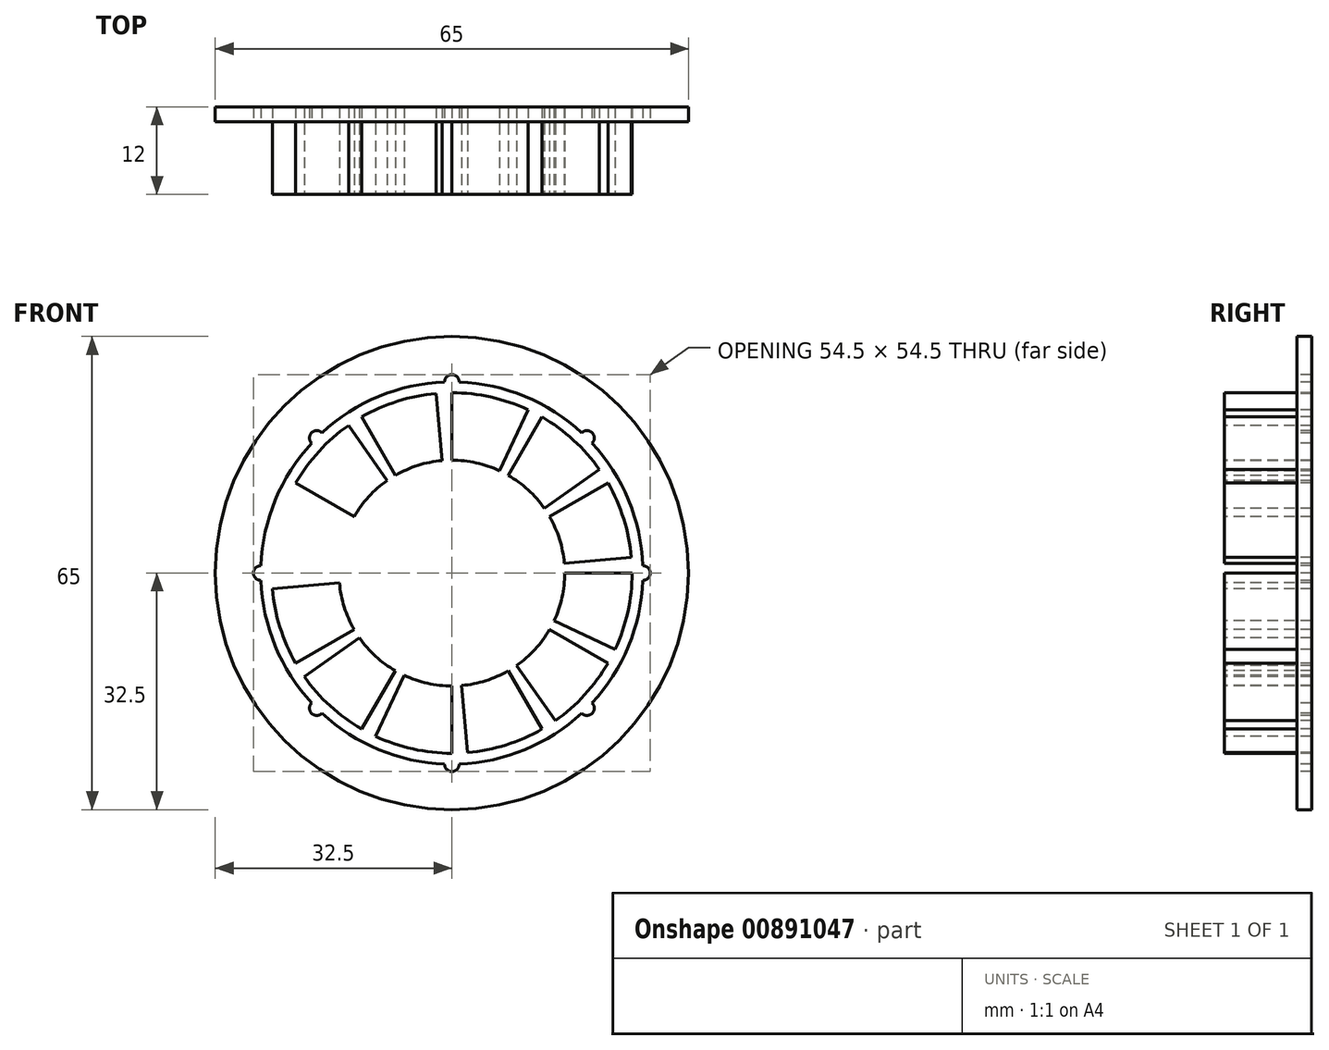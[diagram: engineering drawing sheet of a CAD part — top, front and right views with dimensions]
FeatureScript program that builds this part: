
annotation { "Feature Type Name" : "Feature", "Feature Type Description" : "" }
export const myFeature = defineFeature(function(context is Context, id is Id, definition is map)
    precondition{}
    {
        {
            var Q0;
            Q0=qCreatedBy(makeId("Front.planeOp"),FACE);
            var sketch = newSketch(context, id + "F0", { "sketchPlane" : qUnion([Q0])});
            skCircle(sketch, "E0", {"center": v(0, 0) * mm, "radius": 26.25 * mm});
            skCircle(sketch, "E1", {"center": v(0, 0) * mm, "radius": 14 * mm});
            skSolve(sketch);
        }
        {
            var Q0;
            Q0=makeQuery(id+"F0.imprint","IMPRINT",FACE,{"disambiguationData":[TD([[makeQuery(id+"F0.imprint","IMPRINT",EDGE,{"derivedFrom":sQuery(id+"F0.wireOp",EDGE,"E0")}),1.0]])]});
            extrude(context, id + "F1", {"entities" : qUnion([Q0]), "depth" : 10 * mm, "offsetDistance" : 25 * mm});
        }
        {
            var Q0;
            Q0=qCreatedBy(makeId("Front.planeOp"),FACE);
            var sketch = newSketch(context, id + "F2", { "sketchPlane" : qUnion([Q0])});
            skCircle(sketch, "E2", {"center": v(0, 0) * mm, "radius": 32.5 * mm});
            skCircle(sketch, "E3", {"center": v(0, 0) * mm, "radius": 14 * mm});
            skSolve(sketch);
        }
        {
            var Q0;
            Q0=makeQuery(id+"F2.imprint","IMPRINT",FACE,{"disambiguationData":[TD([[makeQuery(id+"F2.imprint","IMPRINT",EDGE,{"derivedFrom":sQuery(id+"F2.wireOp",EDGE,"E2")}),1.0]])]});
            extrude(context, id + "F3", {"entities" : qUnion([Q0]), "operationType" : NewBodyOperationType.ADD, "oppositeDirection" : true, "depth" : 2 * mm, "offsetDistance" : 25 * mm});
        }
        {
            var Q0;
            Q0=makeQuery(id+"F3.opExtrude","CAP_FACE",FACE,{"disambiguationData":[OSD([sQuery(id+"F2.wireOp",EDGE,"E2"),sQuery(id+"F2.wireOp",EDGE,"E3")])],"isStart":true});
            var sketch = newSketch(context, id + "F4", { "sketchPlane" : qUnion([Q0])});
            skCircle(sketch, "E4", {"center": v(0, 26.25) * mm, "radius": 1 * mm});
            skCircle(sketch, "E5", {"center": v(26.25, 0) * mm, "radius": 1 * mm});
            skCircle(sketch, "E6", {"center": v(0, -26.25) * mm, "radius": 1 * mm});
            skCircle(sketch, "E7", {"center": v(-26.25, 0) * mm, "radius": 1 * mm});
            skCircle(sketch, "E8.1.0", {"center": v(-18.56, 18.56) * mm, "radius": 1 * mm});
            skCircle(sketch, "E8.3.0", {"center": v(-18.56, -18.56) * mm, "radius": 1 * mm});
            skCircle(sketch, "E8.5.0", {"center": v(18.56, -18.56) * mm, "radius": 1 * mm});
            skCircle(sketch, "E8.7.0", {"center": v(18.56, 18.56) * mm, "radius": 1 * mm});
            skPoint(sketch, "E8.center", {"position": v(0, 0) * mm});
            skSolve(sketch);
        }
        {
            var Q0;
            Q0 = qSketchRegion(id + "F4", true);
            var Q1;
            Q1=makeQuery(id+"F1.opExtrude","CAP_FACE",FACE,{"disambiguationData":[OSD([sQuery(id+"F0.wireOp",EDGE,"E0"),sQuery(id+"F0.wireOp",EDGE,"E1")])],"isStart":false});
            extrude(context, id + "F5", {"entities" : qUnion([Q0]), "operationType" : NewBodyOperationType.ADD, "endBound" : BoundingType.UP_TO_SURFACE, "depth" : 25 * mm, "endBoundEntityFace" : qUnion([Q1]), "offsetDistance" : 25 * mm});
        }
        {
            var Q0;
            Q0=makeQuery(id+"F5.boolean.opBoolean","MERGE",FACE,{"derivedFrom":[makeQuery(id+"F1.opExtrude","CAP_FACE",FACE,{"disambiguationData":[OSD([sQuery(id+"F0.wireOp",EDGE,"E0"),sQuery(id+"F0.wireOp",EDGE,"E1")])],"isStart":false}),makeQuery(id+"F5.opExtrude","CAP_FACE",FACE,{"disambiguationData":[OSD([sQuery(id+"F4.wireOp",EDGE,"E4")])],"isStart":false}),makeQuery(id+"F5.opExtrude","CAP_FACE",FACE,{"disambiguationData":[OSD([sQuery(id+"F4.wireOp",EDGE,"E8.1.0")])],"isStart":false}),makeQuery(id+"F5.opExtrude","CAP_FACE",FACE,{"disambiguationData":[OSD([sQuery(id+"F4.wireOp",EDGE,"E7")])],"isStart":false}),makeQuery(id+"F5.opExtrude","CAP_FACE",FACE,{"disambiguationData":[OSD([sQuery(id+"F4.wireOp",EDGE,"E8.3.0")])],"isStart":false}),makeQuery(id+"F5.opExtrude","CAP_FACE",FACE,{"disambiguationData":[OSD([sQuery(id+"F4.wireOp",EDGE,"E6")])],"isStart":false}),makeQuery(id+"F5.opExtrude","CAP_FACE",FACE,{"disambiguationData":[OSD([sQuery(id+"F4.wireOp",EDGE,"E8.5.0")])],"isStart":false}),makeQuery(id+"F5.opExtrude","CAP_FACE",FACE,{"disambiguationData":[OSD([sQuery(id+"F4.wireOp",EDGE,"E5")])],"isStart":false}),makeQuery(id+"F5.opExtrude","CAP_FACE",FACE,{"disambiguationData":[OSD([sQuery(id+"F4.wireOp",EDGE,"E8.7.0")])],"isStart":false})]});
            var sketch = newSketch(context, id + "F6", { "sketchPlane" : qUnion([Q0])});
            skLineSegment(sketch, "E9", {"start": v(-24.75, 0) * mm, "end": v(-15.5, 0) * mm});
            skArc(sketch, "E10", {"start": v(-15.5, 0) * mm, "mid": v(-15.13, 3.35) * mm, "end": v(-14.05, 6.55) * mm});
            skArc(sketch, "E11", {"start": v(-24.75, 0) * mm, "mid": v(-24.16, 5.36) * mm, "end": v(-22.43, 10.46) * mm});
            skLineSegment(sketch, "E12.1.11.0", {"start": v(-22.43, 10.46) * mm, "end": v(-14.05, 6.55) * mm});
            skArc(sketch, "E13.1.0", {"start": v(-21.43, -12.37) * mm, "mid": v(-23.6, -7.44) * mm, "end": v(-24.66, -2.16) * mm});
            skLineSegment(sketch, "E13.1.1", {"start": v(-21.43, -12.37) * mm, "end": v(-13.42, -7.75) * mm});
            skLineSegment(sketch, "E13.1.2", {"start": v(-24.66, -2.16) * mm, "end": v(-15.44, -1.35) * mm});
            skArc(sketch, "E13.1.3", {"start": v(-13.42, -7.75) * mm, "mid": v(-14.78, -4.66) * mm, "end": v(-15.44, -1.35) * mm});
            skArc(sketch, "E13.2.0", {"start": v(-12.38, -21.43) * mm, "mid": v(-16.72, -18.25) * mm, "end": v(-20.27, -14.2) * mm});
            skLineSegment(sketch, "E13.2.1", {"start": v(-12.38, -21.43) * mm, "end": v(-7.75, -13.42) * mm});
            skLineSegment(sketch, "E13.2.2", {"start": v(-20.27, -14.2) * mm, "end": v(-12.7, -8.9) * mm});
            skArc(sketch, "E13.2.3", {"start": v(-7.75, -13.42) * mm, "mid": v(-10.47, -11.43) * mm, "end": v(-12.7, -8.9) * mm});
            skArc(sketch, "E13.3.0", {"start": v(0, -24.75) * mm, "mid": v(-5.36, -24.16) * mm, "end": v(-10.46, -22.43) * mm});
            skLineSegment(sketch, "E13.3.1", {"start": v(0, -24.75) * mm, "end": v(0, -15.5) * mm});
            skLineSegment(sketch, "E13.3.2", {"start": v(-10.46, -22.43) * mm, "end": v(-6.55, -14.05) * mm});
            skArc(sketch, "E13.3.3", {"start": v(0, -15.5) * mm, "mid": v(-3.35, -15.13) * mm, "end": v(-6.55, -14.05) * mm});
            skArc(sketch, "E13.4.0", {"start": v(12.37, -21.43) * mm, "mid": v(7.44, -23.6) * mm, "end": v(2.16, -24.66) * mm});
            skLineSegment(sketch, "E13.4.1", {"start": v(12.37, -21.43) * mm, "end": v(7.75, -13.42) * mm});
            skLineSegment(sketch, "E13.4.2", {"start": v(2.16, -24.66) * mm, "end": v(1.35, -15.44) * mm});
            skArc(sketch, "E13.4.3", {"start": v(7.75, -13.42) * mm, "mid": v(4.66, -14.78) * mm, "end": v(1.35, -15.44) * mm});
            skArc(sketch, "E13.5.0", {"start": v(21.43, -12.37) * mm, "mid": v(18.25, -16.72) * mm, "end": v(14.2, -20.27) * mm});
            skLineSegment(sketch, "E13.5.1", {"start": v(21.43, -12.37) * mm, "end": v(13.42, -7.75) * mm});
            skLineSegment(sketch, "E13.5.2", {"start": v(14.2, -20.27) * mm, "end": v(8.9, -12.7) * mm});
            skArc(sketch, "E13.5.3", {"start": v(13.42, -7.75) * mm, "mid": v(11.43, -10.47) * mm, "end": v(8.9, -12.7) * mm});
            skArc(sketch, "E13.6.0", {"start": v(24.75, 0) * mm, "mid": v(24.16, -5.36) * mm, "end": v(22.43, -10.46) * mm});
            skLineSegment(sketch, "E13.6.1", {"start": v(24.75, 0) * mm, "end": v(15.5, 0) * mm});
            skLineSegment(sketch, "E13.6.2", {"start": v(22.43, -10.46) * mm, "end": v(14.05, -6.55) * mm});
            skArc(sketch, "E13.6.3", {"start": v(15.5, 0) * mm, "mid": v(15.13, -3.35) * mm, "end": v(14.05, -6.55) * mm});
            skArc(sketch, "E13.7.0", {"start": v(21.43, 12.37) * mm, "mid": v(23.6, 7.44) * mm, "end": v(24.66, 2.16) * mm});
            skLineSegment(sketch, "E13.7.1", {"start": v(21.43, 12.37) * mm, "end": v(13.42, 7.75) * mm});
            skLineSegment(sketch, "E13.7.2", {"start": v(24.66, 2.16) * mm, "end": v(15.44, 1.35) * mm});
            skArc(sketch, "E13.7.3", {"start": v(13.42, 7.75) * mm, "mid": v(14.78, 4.66) * mm, "end": v(15.44, 1.35) * mm});
            skArc(sketch, "E13.8.0", {"start": v(12.38, 21.43) * mm, "mid": v(16.72, 18.25) * mm, "end": v(20.27, 14.2) * mm});
            skLineSegment(sketch, "E13.8.1", {"start": v(12.38, 21.43) * mm, "end": v(7.75, 13.42) * mm});
            skLineSegment(sketch, "E13.8.2", {"start": v(20.27, 14.2) * mm, "end": v(12.7, 8.9) * mm});
            skArc(sketch, "E13.8.3", {"start": v(7.75, 13.42) * mm, "mid": v(10.47, 11.43) * mm, "end": v(12.7, 8.9) * mm});
            skArc(sketch, "E13.9.0", {"start": v(0, 24.75) * mm, "mid": v(5.36, 24.16) * mm, "end": v(10.46, 22.43) * mm});
            skLineSegment(sketch, "E13.9.1", {"start": v(0, 24.75) * mm, "end": v(0, 15.5) * mm});
            skLineSegment(sketch, "E13.9.2", {"start": v(10.46, 22.43) * mm, "end": v(6.55, 14.05) * mm});
            skArc(sketch, "E13.9.3", {"start": v(0, 15.5) * mm, "mid": v(3.35, 15.13) * mm, "end": v(6.55, 14.05) * mm});
            skArc(sketch, "E13.10.0", {"start": v(-12.37, 21.43) * mm, "mid": v(-7.44, 23.6) * mm, "end": v(-2.16, 24.66) * mm});
            skLineSegment(sketch, "E13.10.1", {"start": v(-12.38, 21.43) * mm, "end": v(-7.75, 13.42) * mm});
            skLineSegment(sketch, "E13.10.2", {"start": v(-2.16, 24.66) * mm, "end": v(-1.35, 15.44) * mm});
            skArc(sketch, "E13.10.3", {"start": v(-7.75, 13.42) * mm, "mid": v(-4.66, 14.78) * mm, "end": v(-1.35, 15.44) * mm});
            skArc(sketch, "E13.11.0", {"start": v(-21.43, 12.38) * mm, "mid": v(-18.25, 16.72) * mm, "end": v(-14.2, 20.27) * mm});
            skLineSegment(sketch, "E13.11.1", {"start": v(-21.43, 12.38) * mm, "end": v(-13.42, 7.75) * mm});
            skLineSegment(sketch, "E13.11.2", {"start": v(-14.2, 20.27) * mm, "end": v(-8.9, 12.7) * mm});
            skArc(sketch, "E13.11.3", {"start": v(-13.42, 7.75) * mm, "mid": v(-11.43, 10.47) * mm, "end": v(-8.9, 12.7) * mm});
            skSolve(sketch);
        }
        {
            var Q0;
            Q0=makeQuery(id+"F6.imprint","IMPRINT",FACE,{"disambiguationData":[TD([[makeQuery(id+"F6.imprint","IMPRINT",EDGE,{"derivedFrom":sQuery(id+"F6.wireOp",EDGE,"E13.1.0")}),-1.0]])]});
            var Q1;
            Q1=makeQuery(id+"F6.imprint","IMPRINT",FACE,{"disambiguationData":[TD([[makeQuery(id+"F6.imprint","IMPRINT",EDGE,{"derivedFrom":sQuery(id+"F6.wireOp",EDGE,"E13.2.0")}),-1.0]])]});
            var Q2;
            Q2=makeQuery(id+"F6.imprint","IMPRINT",FACE,{"disambiguationData":[TD([[makeQuery(id+"F6.imprint","IMPRINT",EDGE,{"derivedFrom":sQuery(id+"F6.wireOp",EDGE,"E13.3.0")}),-1.0]])]});
            var Q3;
            Q3=makeQuery(id+"F6.imprint","IMPRINT",FACE,{"disambiguationData":[TD([[makeQuery(id+"F6.imprint","IMPRINT",EDGE,{"derivedFrom":sQuery(id+"F6.wireOp",EDGE,"E13.4.0")}),-1.0]])]});
            var Q4;
            Q4=makeQuery(id+"F6.imprint","IMPRINT",FACE,{"disambiguationData":[TD([[makeQuery(id+"F6.imprint","IMPRINT",EDGE,{"derivedFrom":sQuery(id+"F6.wireOp",EDGE,"E13.5.0")}),-1.0]])]});
            var Q5;
            Q5=makeQuery(id+"F6.imprint","IMPRINT",FACE,{"disambiguationData":[TD([[makeQuery(id+"F6.imprint","IMPRINT",EDGE,{"derivedFrom":sQuery(id+"F6.wireOp",EDGE,"E13.6.0")}),-1.0]])]});
            var Q6;
            Q6=makeQuery(id+"F6.imprint","IMPRINT",FACE,{"disambiguationData":[TD([[makeQuery(id+"F6.imprint","IMPRINT",EDGE,{"derivedFrom":sQuery(id+"F6.wireOp",EDGE,"E13.7.0")}),-1.0]])]});
            var Q7;
            Q7=makeQuery(id+"F6.imprint","IMPRINT",FACE,{"disambiguationData":[TD([[makeQuery(id+"F6.imprint","IMPRINT",EDGE,{"derivedFrom":sQuery(id+"F6.wireOp",EDGE,"E13.8.0")}),-1.0]])]});
            var Q8;
            Q8=makeQuery(id+"F6.imprint","IMPRINT",FACE,{"disambiguationData":[TD([[makeQuery(id+"F6.imprint","IMPRINT",EDGE,{"derivedFrom":sQuery(id+"F6.wireOp",EDGE,"E13.9.0")}),-1.0]])]});
            var Q9;
            Q9=makeQuery(id+"F6.imprint","IMPRINT",FACE,{"disambiguationData":[TD([[makeQuery(id+"F6.imprint","IMPRINT",EDGE,{"derivedFrom":sQuery(id+"F6.wireOp",EDGE,"E13.10.0")}),-1.0]])]});
            var Q10;
            Q10=makeQuery(id+"F6.imprint","IMPRINT",FACE,{"disambiguationData":[TD([[makeQuery(id+"F6.imprint","IMPRINT",EDGE,{"derivedFrom":sQuery(id+"F6.wireOp",EDGE,"E13.11.0")}),-1.0]])]});
            var Q11;
            Q11=makeQuery(id+"F6.imprint","IMPRINT",FACE,{"disambiguationData":[TD([[makeQuery(id+"F6.imprint","IMPRINT",EDGE,{"derivedFrom":sQuery(id+"F6.wireOp",EDGE,"E9")}),1.0]])]});
            extrude(context, id + "F7", {"entities" : qUnion([Q0, Q1, Q2, Q3, Q4, Q5, Q6, Q7, Q8, Q9, Q10, Q11]), "operationType" : NewBodyOperationType.REMOVE, "oppositeDirection" : true, "depth" : 25 * mm, "offsetDistance" : 25 * mm});
        }
    });
